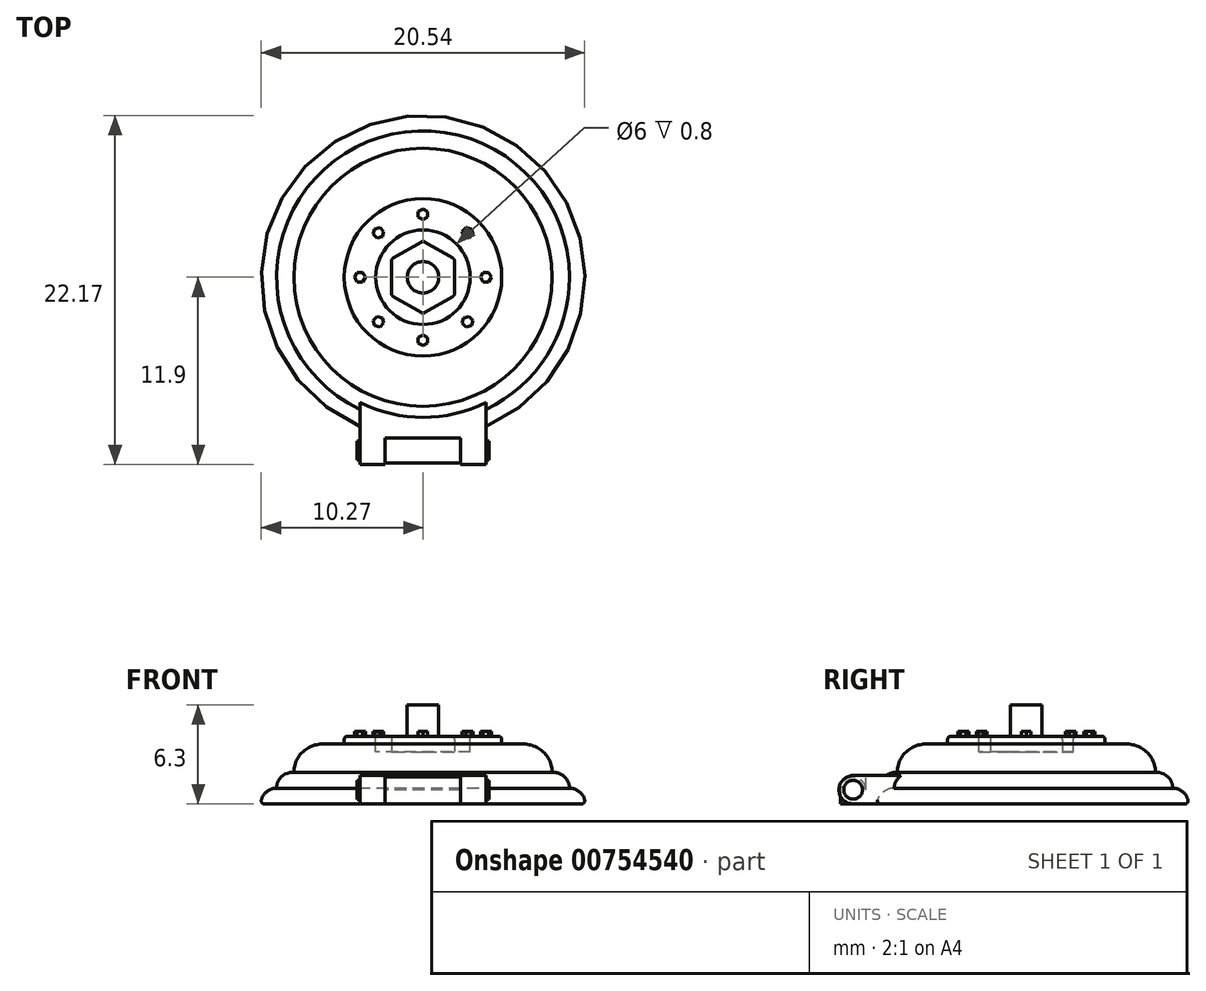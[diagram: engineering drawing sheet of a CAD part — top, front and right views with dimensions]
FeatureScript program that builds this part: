
annotation { "Feature Type Name" : "Feature", "Feature Type Description" : "" }
export const myFeature = defineFeature(function(context is Context, id is Id, definition is map)
    precondition{}
    {
        {
            var Q0;
            Q0=qCreatedBy(makeId("Right.planeOp"),FACE);
            var sketch = newSketch(context, id + "F0", { "sketchPlane" : qUnion([Q0])});
            skLineSegment(sketch, "E0", {"start": v(0, 0) * mm, "end": v(10.3, 0) * mm});
            skArc(sketch, "E1", {"start": v(9.3, 1) * mm, "mid": v(9, 1.7) * mm, "end": v(8.3, 2) * mm});
            skLineSegment(sketch, "E2", {"start": v(8.3, 2) * mm, "end": v(5, 2) * mm});
            skLineSegment(sketch, "E3", {"start": v(5, 2) * mm, "end": v(5, 4.3) * mm});
            skLineSegment(sketch, "E4", {"start": v(5, 4.3) * mm, "end": v(3, 4.3) * mm});
            skLineSegment(sketch, "E5", {"start": v(3, 4.3) * mm, "end": v(3, 3.3) * mm});
            skLineSegment(sketch, "E6", {"start": v(3, 3.3) * mm, "end": v(0, 3.3) * mm});
            skLineSegment(sketch, "E7", {"start": v(0, 3.3) * mm, "end": v(0, 0) * mm});
            skArc(sketch, "E8", {"start": v(10.3, 0) * mm, "mid": v(10, 0.7) * mm, "end": v(9.3, 1) * mm});
            skSolve(sketch);
        }
        {
            var Q0;
            Q0=makeQuery(id+"F0.imprint","IMPRINT",FACE,{"disambiguationData":[TD([[makeQuery(id+"F0.imprint","IMPRINT",EDGE,{"derivedFrom":sQuery(id+"F0.wireOp",EDGE,"E0")}),1.0]])]});
            var Q1;
            Q1=sQuery(id+"F0.wireOp",EDGE,"E7");
            revolve(context, id + "F1", {"surfaceOperationType" : NewSurfaceOperationType.NEW, "entities" : qUnion([Q0]), "axis" : qUnion([Q1]), "revolveType" : RevolveType.FULL});
        }
        {
            var Q0;
            Q0=makeQuery(id+"F1.opRevolve","SWEPT_FACE",FACE,{"disambiguationData":[OSD([sQuery(id+"F0.wireOp",EDGE,"E6")])]});
            var sketch = newSketch(context, id + "F2", { "sketchPlane" : qUnion([Q0])});
            skCircle(sketch, "E9.cCircle", {"center": v(0, 0) * mm, "radius": 2 * mm, "construction": true});
            skLineSegment(sketch, "E9.0", {"start": v(0, 2.3) * mm, "end": v(2, 1.15) * mm});
            skLineSegment(sketch, "E9.1", {"start": v(2, 1.15) * mm, "end": v(2, -1.15) * mm});
            skLineSegment(sketch, "E9.2", {"start": v(2, -1.15) * mm, "end": v(0, -2.3) * mm});
            skLineSegment(sketch, "E9.3", {"start": v(0, -2.3) * mm, "end": v(-2, -1.15) * mm});
            skLineSegment(sketch, "E9.4", {"start": v(-2, -1.15) * mm, "end": v(-2, 1.15) * mm});
            skLineSegment(sketch, "E9.5", {"start": v(-2, 1.15) * mm, "end": v(0, 2.3) * mm});
            skPoint(sketch, "E9.0.midPoint", {"position": v(1, 1.73) * mm});
            skSolve(sketch);
        }
        {
            var Q0;
            Q0=makeQuery(id+"F2.imprint","IMPRINT",FACE,{"disambiguationData":[TD([[makeQuery(id+"F2.imprint","IMPRINT",EDGE,{"derivedFrom":sQuery(id+"F2.wireOp",EDGE,"E9.0")}),-1.0]])]});
            extrude(context, id + "F3", {"entities" : qUnion([Q0]), "operationType" : NewBodyOperationType.ADD, "depth" : 1 * mm, "offsetDistance" : 25 * mm});
        }
        {
            var Q0;
            Q0=makeQuery(id+"F3.opExtrude","CAP_FACE",FACE,{"disambiguationData":[OSD([sQuery(id+"F2.wireOp",EDGE,"E9.0"),sQuery(id+"F2.wireOp",EDGE,"E9.1"),sQuery(id+"F2.wireOp",EDGE,"E9.2"),sQuery(id+"F2.wireOp",EDGE,"E9.3"),sQuery(id+"F2.wireOp",EDGE,"E9.4"),sQuery(id+"F2.wireOp",EDGE,"E9.5")])],"isStart":false});
            var Q1;
            Q1=makeQuery(id+"F1.opRevolve","SWEPT_FACE",FACE,{"disambiguationData":[OSD([sQuery(id+"F0.wireOp",EDGE,"E4")])]});
            var Q2;
            Q2=makeQuery(id+"F3.opExtrude","SWEPT_EDGE",EDGE,{"disambiguationData":[OSD([sQuery(id+"F2.wireOp",EDGE,"E9.2"),sQuery(id+"F2.wireOp",EDGE,"E9.3")])]});
            var Q3;
            Q3=makeQuery(id+"F3.opExtrude","SWEPT_EDGE",EDGE,{"disambiguationData":[OSD([sQuery(id+"F2.wireOp",EDGE,"E9.3"),sQuery(id+"F2.wireOp",EDGE,"E9.4")])]});
            var Q4;
            Q4=makeQuery(id+"F3.opExtrude","SWEPT_EDGE",EDGE,{"disambiguationData":[OSD([sQuery(id+"F2.wireOp",EDGE,"E9.1"),sQuery(id+"F2.wireOp",EDGE,"E9.2")])]});
            var Q5;
            Q5=makeQuery(id+"F3.opExtrude","SWEPT_EDGE",EDGE,{"disambiguationData":[OSD([sQuery(id+"F2.wireOp",EDGE,"E9.0"),sQuery(id+"F2.wireOp",EDGE,"E9.1")])]});
            var Q6;
            Q6=makeQuery(id+"F1.opRevolve","SWEPT_EDGE",EDGE,{"disambiguationData":[OSD([sQuery(id+"F0.wireOp",EDGE,"E0"),sQuery(id+"F0.wireOp",EDGE,"84ipGY4g-S0fZ-bzdn-T0Xh-eLM8dJ8qEPkn")])]});
            var Q7;
            Q7=makeQuery(id+"F3.opExtrude","SWEPT_EDGE",EDGE,{"disambiguationData":[OSD([sQuery(id+"F2.wireOp",EDGE,"E9.0"),sQuery(id+"F2.wireOp",EDGE,"E9.5")])]});
            var Q8;
            Q8=makeQuery(id+"F3.opExtrude","SWEPT_EDGE",EDGE,{"disambiguationData":[OSD([sQuery(id+"F2.wireOp",EDGE,"E9.4"),sQuery(id+"F2.wireOp",EDGE,"E9.5")])]});
            fillet(context, id + "F4", {"entities" : qUnion([Q0, Q1, Q2, Q3, Q4, Q5, Q6, Q7, Q8]), "radius" : 0.2 * mm, "tangentPropagation" : true, "defaultsChanged" : false, "vertexSettings" : [], "allowEdgeOverflow" : false});
        }
        {
            var Q0;
            Q0=makeQuery(id+"F3.opExtrude","CAP_FACE",FACE,{"disambiguationData":[OSD([sQuery(id+"F2.wireOp",EDGE,"E9.0"),sQuery(id+"F2.wireOp",EDGE,"E9.1"),sQuery(id+"F2.wireOp",EDGE,"E9.2"),sQuery(id+"F2.wireOp",EDGE,"E9.3"),sQuery(id+"F2.wireOp",EDGE,"E9.4"),sQuery(id+"F2.wireOp",EDGE,"E9.5")])],"isStart":false});
            var sketch = newSketch(context, id + "F5", { "sketchPlane" : qUnion([Q0])});
            skCircle(sketch, "E10", {"center": v(0, 0) * mm, "radius": 1 * mm});
            skSolve(sketch);
        }
        {
            var Q0;
            Q0=makeQuery(id+"F5.imprint","IMPRINT",FACE,{"disambiguationData":[TD([[makeQuery(id+"F5.imprint","IMPRINT",EDGE,{"derivedFrom":sQuery(id+"F5.wireOp",EDGE,"E10")}),1.0]])]});
            var Q1;
            Q1 = qSketchRegion(id + "F7", true);
            extrude(context, id + "F6", {"entities" : qUnion([Q0, Q1]), "operationType" : NewBodyOperationType.ADD, "depth" : 2 * mm, "offsetDistance" : 25 * mm});
        }
        {
            var Q0;
            Q0=makeQuery(id+"F1.opRevolve","SWEPT_FACE",FACE,{"disambiguationData":[OSD([sQuery(id+"F0.wireOp",EDGE,"E4")])]});
            var sketch = newSketch(context, id + "F7", { "sketchPlane" : qUnion([Q0])});
            skCircle(sketch, "E11.cCircle", {"center": v(0, 4) * mm, "radius": 0.3 * mm});
            skLineSegment(sketch, "E11.0", {"start": v(0, 4.35) * mm, "end": v(0.3, 4.17) * mm});
            skLineSegment(sketch, "E11.1", {"start": v(0.3, 4.17) * mm, "end": v(0.3, 3.83) * mm});
            skLineSegment(sketch, "E11.2", {"start": v(0.3, 3.83) * mm, "end": v(0, 3.65) * mm});
            skLineSegment(sketch, "E11.3", {"start": v(0, 3.65) * mm, "end": v(-0.3, 3.83) * mm});
            skLineSegment(sketch, "E11.4", {"start": v(-0.3, 3.83) * mm, "end": v(-0.3, 4.17) * mm});
            skLineSegment(sketch, "E11.5", {"start": v(-0.3, 4.17) * mm, "end": v(0, 4.35) * mm});
            skSolve(sketch);
        }
        {
            var Q0;
            {var subQ0=sQuery(id+"F7.wireOp",EDGE,"E11.4");var subQ1=sQuery(id+"F7.wireOp",EDGE,"E11.cCircle");var subQ2=makeQuery(id+"F7.imprint","INTERSECT",VERTEX,{"derivedFrom":[subQ1,subQ0]});Q0=makeQuery(id+"F7.imprint","IMPRINT",FACE,{"disambiguationData":[TD([[makeQuery(id+"F7.imprint","IMPRINT",EDGE,{"disambiguationData":[TD([[subQ2,-1.0]])],"derivedFrom":subQ1}),-1.0]])]});}
            var Q1;
            {var subQ0=sQuery(id+"F7.wireOp",EDGE,"E11.3");var subQ1=sQuery(id+"F7.wireOp",EDGE,"E11.cCircle");var subQ2=makeQuery(id+"F7.imprint","INTERSECT",VERTEX,{"derivedFrom":[subQ1,subQ0]});Q1=makeQuery(id+"F7.imprint","IMPRINT",FACE,{"disambiguationData":[TD([[makeQuery(id+"F7.imprint","IMPRINT",EDGE,{"disambiguationData":[TD([[subQ2,-1.0]])],"derivedFrom":subQ1}),-1.0]])]});}
            var Q2;
            {var subQ0=sQuery(id+"F7.wireOp",EDGE,"E11.1");var subQ1=sQuery(id+"F7.wireOp",EDGE,"E11.cCircle");var subQ2=makeQuery(id+"F7.imprint","INTERSECT",VERTEX,{"derivedFrom":[subQ1,subQ0]});Q2=makeQuery(id+"F7.imprint","IMPRINT",FACE,{"disambiguationData":[TD([[makeQuery(id+"F7.imprint","IMPRINT",EDGE,{"disambiguationData":[TD([[subQ2,1.0]])],"derivedFrom":subQ1}),-1.0]])]});}
            var Q3;
            {var subQ0=sQuery(id+"F7.wireOp",EDGE,"E11.5");var subQ1=sQuery(id+"F7.wireOp",EDGE,"E11.cCircle");var subQ2=makeQuery(id+"F7.imprint","INTERSECT",VERTEX,{"derivedFrom":[subQ1,subQ0]});Q3=makeQuery(id+"F7.imprint","IMPRINT",FACE,{"disambiguationData":[TD([[makeQuery(id+"F7.imprint","IMPRINT",EDGE,{"disambiguationData":[TD([[subQ2,-1.0]])],"derivedFrom":subQ1}),-1.0]])]});}
            var Q4;
            {var subQ0=sQuery(id+"F7.wireOp",EDGE,"E11.0");var subQ1=sQuery(id+"F7.wireOp",EDGE,"E11.cCircle");var subQ2=makeQuery(id+"F7.imprint","INTERSECT",VERTEX,{"derivedFrom":[subQ1,subQ0]});Q4=makeQuery(id+"F7.imprint","IMPRINT",FACE,{"disambiguationData":[TD([[makeQuery(id+"F7.imprint","IMPRINT",EDGE,{"disambiguationData":[TD([[subQ2,-1.0]])],"derivedFrom":subQ1}),-1.0]])]});}
            var Q5;
            {var subQ0=sQuery(id+"F7.wireOp",EDGE,"E11.0");var subQ1=sQuery(id+"F7.wireOp",EDGE,"E11.cCircle");var subQ2=makeQuery(id+"F7.imprint","INTERSECT",VERTEX,{"derivedFrom":[subQ1,subQ0]});Q5=makeQuery(id+"F7.imprint","IMPRINT",FACE,{"disambiguationData":[TD([[makeQuery(id+"F7.imprint","IMPRINT",EDGE,{"disambiguationData":[TD([[subQ2,1.0]])],"derivedFrom":subQ1}),-1.0]])]});}
            var Q6;
            {var subQ0=sQuery(id+"F7.wireOp",EDGE,"E11.cCircle");var subQ4=makeQuery(id+"F7.imprint","INTERSECT",VERTEX,{"derivedFrom":[subQ0,sQuery(id+"F7.wireOp",EDGE,"E11.0")]});Q6=makeQuery(id+"F7.imprint","IMPRINT",FACE,{"disambiguationData":[TD([[makeQuery(id+"F7.imprint","IMPRINT",EDGE,{"disambiguationData":[TD([[subQ4,1.0]])],"derivedFrom":subQ0}),1.0]])]});}
            var Q7;
            Q7=sQuery(id+"F7.wireOp",EDGE,"E11.4");
            var Q8;
            Q8=sQuery(id+"F7.wireOp",EDGE,"E11.3");
            var Q9;
            Q9=sQuery(id+"F7.wireOp",EDGE,"E11.2");
            var Q10;
            Q10=sQuery(id+"F7.wireOp",EDGE,"E11.1");
            var Q11;
            Q11=sQuery(id+"F7.wireOp",EDGE,"E11.0");
            var Q12;
            Q12=sQuery(id+"F7.wireOp",EDGE,"E11.5");
            extrude(context, id + "F8", {"entities" : qUnion([Q0, Q1, Q2, Q3, Q4, Q5, Q6]), "surfaceEntities" : qUnion([Q7, Q8, Q9, Q10, Q11, Q12]), "depth" : 0.3 * mm, "offsetDistance" : 25 * mm});
        }
        {
            var Q0;
            Q0=makeQuery(id+"F8.opExtrude","SWEPT_BODY",BODY,{"disambiguationData":[OSD([sQuery(id+"F7.wireOp",EDGE,"E11.0"),sQuery(id+"F7.wireOp",EDGE,"E11.1"),sQuery(id+"F7.wireOp",EDGE,"E11.2"),sQuery(id+"F7.wireOp",EDGE,"E11.3"),sQuery(id+"F7.wireOp",EDGE,"E11.4"),sQuery(id+"F7.wireOp",EDGE,"E11.5")])]});
            var Q1;
            {var subQ0=sQuery(id+"F0.wireOp",EDGE,"E4");Q1=makeQuery(id+"F4.opFillet","BLEND_EDGE",EDGE,{"blendedFrom":[makeQuery(id+"F1.opRevolve","SWEPT_EDGE",EDGE,{"disambiguationData":[OSD([subQ0,sQuery(id+"F0.wireOp",EDGE,"E5")])]}),makeQuery(id+"F1.opRevolve","SWEPT_FACE",FACE,{"disambiguationData":[OSD([subQ0])]})],"blendedInto":[makeQuery(id+"F1.opRevolve","SWEPT_FACE",FACE,{"disambiguationData":[OSD([subQ0])]})]});}
            circularPattern(context, id + "F9", {"operationType" : NewBodyOperationType.ADD, "entities" : qUnion([Q0]), "axis" : qUnion([Q1]), "angle" : 360 * degree, "instanceCount" : 8, "equalSpace" : true});
        }
        {
            var Q0;
            Q0=qCreatedBy(makeId("Right.planeOp"),FACE);
            var sketch = newSketch(context, id + "F10", { "sketchPlane" : qUnion([Q0])});
            skLineSegment(sketch, "E12", {"start": v(-4, 0) * mm, "end": v(-11, 0) * mm});
            skArc(sketch, "E13", {"start": v(-11, 1.8) * mm, "mid": v(-11.9, 0.9) * mm, "end": v(-11, 0) * mm});
            skLineSegment(sketch, "E14", {"start": v(-11, 1.8) * mm, "end": v(-4, 1.8) * mm});
            skLineSegment(sketch, "E15", {"start": v(-4, 1.8) * mm, "end": v(-4, 0) * mm});
            skArc(sketch, "E16", {"start": v(-11, 0) * mm, "mid": v(-10.1, 0.9) * mm, "end": v(-11, 1.8) * mm, "construction": true});
            skSolve(sketch);
        }
        {
            var Q0;
            Q0=makeQuery(id+"F10.imprint","IMPRINT",FACE,{"disambiguationData":[TD([[makeQuery(id+"F10.imprint","IMPRINT",EDGE,{"derivedFrom":sQuery(id+"F10.wireOp",EDGE,"E12")}),-1.0]])]});
            extrude(context, id + "F11", {"entities" : qUnion([Q0]), "operationType" : NewBodyOperationType.ADD, "endBound" : BoundingType.SYMMETRIC, "depth" : 8 * mm, "offsetDistance" : 25 * mm});
        }
        {
            var Q0;
            Q0=makeQuery(id+"F11.opExtrude","SWEPT_FACE",FACE,{"disambiguationData":[OSD([sQuery(id+"F10.wireOp",EDGE,"E14")])]});
            var sketch = newSketch(context, id + "F12", { "sketchPlane" : qUnion([Q0])});
            skLineSegment(sketch, "E17.bottom", {"start": v(-2.4, -10.2) * mm, "end": v(2.4, -10.2) * mm});
            skLineSegment(sketch, "E17.top", {"start": v(-2.4, -15.2) * mm, "end": v(2.4, -15.2) * mm});
            skLineSegment(sketch, "E17.left", {"start": v(-2.4, -10.2) * mm, "end": v(-2.4, -15.2) * mm});
            skLineSegment(sketch, "E17.right", {"start": v(2.4, -10.2) * mm, "end": v(2.4, -15.2) * mm});
            skSolve(sketch);
        }
        {
            var Q0;
            {var subQ0=sQuery(id+"F12.wireOp",EDGE,"E17.bottom");Q0=makeQuery(id+"F12.imprint","IMPRINT",FACE,{"disambiguationData":[TD([[makeQuery(id+"F12.imprint","IMPRINT",EDGE,{"derivedFrom":subQ0}),-1.0]])]});}
            var Q1;
            {var subQ0=sQuery(id+"F12.wireOp",EDGE,"E17.top");Q1=makeQuery(id+"F12.imprint","IMPRINT",FACE,{"disambiguationData":[TD([[makeQuery(id+"F12.imprint","IMPRINT",EDGE,{"derivedFrom":subQ0}),1.0]])]});}
            extrude(context, id + "F13", {"entities" : qUnion([Q0, Q1]), "operationType" : NewBodyOperationType.REMOVE, "endBound" : BoundingType.THROUGH_ALL, "oppositeDirection" : true, "depth" : 25 * mm, "offsetDistance" : 25 * mm});
        }
        {
            var Q0;
            Q0=qCreatedBy(makeId("Right.planeOp"),FACE);
            var sketch = newSketch(context, id + "F14", { "sketchPlane" : qUnion([Q0])});
            skCircle(sketch, "E18", {"center": v(-11, 0.9) * mm, "radius": 0.6 * mm});
            skSolve(sketch);
        }
        {
            var Q0;
            Q0=makeQuery(id+"F14.imprint","IMPRINT",FACE,{"disambiguationData":[TD([[makeQuery(id+"F14.imprint","IMPRINT",EDGE,{"derivedFrom":sQuery(id+"F14.wireOp",EDGE,"E18")}),1.0]])]});
            extrude(context, id + "F15", {"entities" : qUnion([Q0]), "operationType" : NewBodyOperationType.ADD, "endBound" : BoundingType.SYMMETRIC, "depth" : 8.4 * mm, "offsetDistance" : 25 * mm});
        }
        {
            var Q0;
            Q0=qCreatedBy(makeId("Right.planeOp"),FACE);
            var sketch = newSketch(context, id + "F16", { "sketchPlane" : qUnion([Q0])});
            skArc(sketch, "E19", {"start": v(-10.2, 0.9) * mm, "mid": v(-11, 1.7) * mm, "end": v(-11.8, 0.9) * mm});
            skLineSegment(sketch, "E20", {"start": v(-11.8, 0.9) * mm, "end": v(-11.8, 0) * mm});
            skLineSegment(sketch, "E21", {"start": v(-11.8, 0) * mm, "end": v(-10.2, 0) * mm});
            skLineSegment(sketch, "E22", {"start": v(-10.2, 0) * mm, "end": v(-10.2, 0.9) * mm});
            skSolve(sketch);
        }
        {
            var Q0;
            Q0=makeQuery(id+"F16.imprint","IMPRINT",FACE,{"disambiguationData":[TD([[makeQuery(id+"F16.imprint","IMPRINT",EDGE,{"derivedFrom":sQuery(id+"F16.wireOp",EDGE,"E19")}),1.0]])]});
            extrude(context, id + "F17", {"entities" : qUnion([Q0]), "operationType" : NewBodyOperationType.ADD, "endBound" : BoundingType.SYMMETRIC, "depth" : 4.8 * mm, "offsetDistance" : 25 * mm});
        }
        {
            var Q0;
            Q0=qCreatedBy(makeId("Right.planeOp"),FACE);
            var sketch = newSketch(context, id + "F18", { "sketchPlane" : qUnion([Q0])});
            skArc(sketch, "E23", {"start": v(8.2, 2) * mm, "mid": v(7.67, 3.27) * mm, "end": v(6.4, 3.8) * mm});
            skLineSegment(sketch, "E24", {"start": v(6.4, 3.8) * mm, "end": v(4, 3.8) * mm});
            skLineSegment(sketch, "E25", {"start": v(4, 3.8) * mm, "end": v(4, 2) * mm});
            skLineSegment(sketch, "E26", {"start": v(0, 0) * mm, "end": v(0, 6) * mm, "construction": true});
            skLineSegment(sketch, "E27", {"start": v(4, 2) * mm, "end": v(8.2, 2) * mm});
            skSolve(sketch);
        }
        {
            var Q0;
            Q0=makeQuery(id+"F18.imprint","IMPRINT",FACE,{"disambiguationData":[TD([[makeQuery(id+"F18.imprint","IMPRINT",EDGE,{"derivedFrom":sQuery(id+"F18.wireOp",EDGE,"E23")}),1.0]])]});
            var Q1;
            Q1=sQuery(id+"F18.wireOp",EDGE,"E26");
            revolve(context, id + "F19", {"operationType" : NewBodyOperationType.ADD, "surfaceOperationType" : NewSurfaceOperationType.NEW, "entities" : qUnion([Q0]), "axis" : qUnion([Q1]), "revolveType" : RevolveType.FULL});
        }
    });
